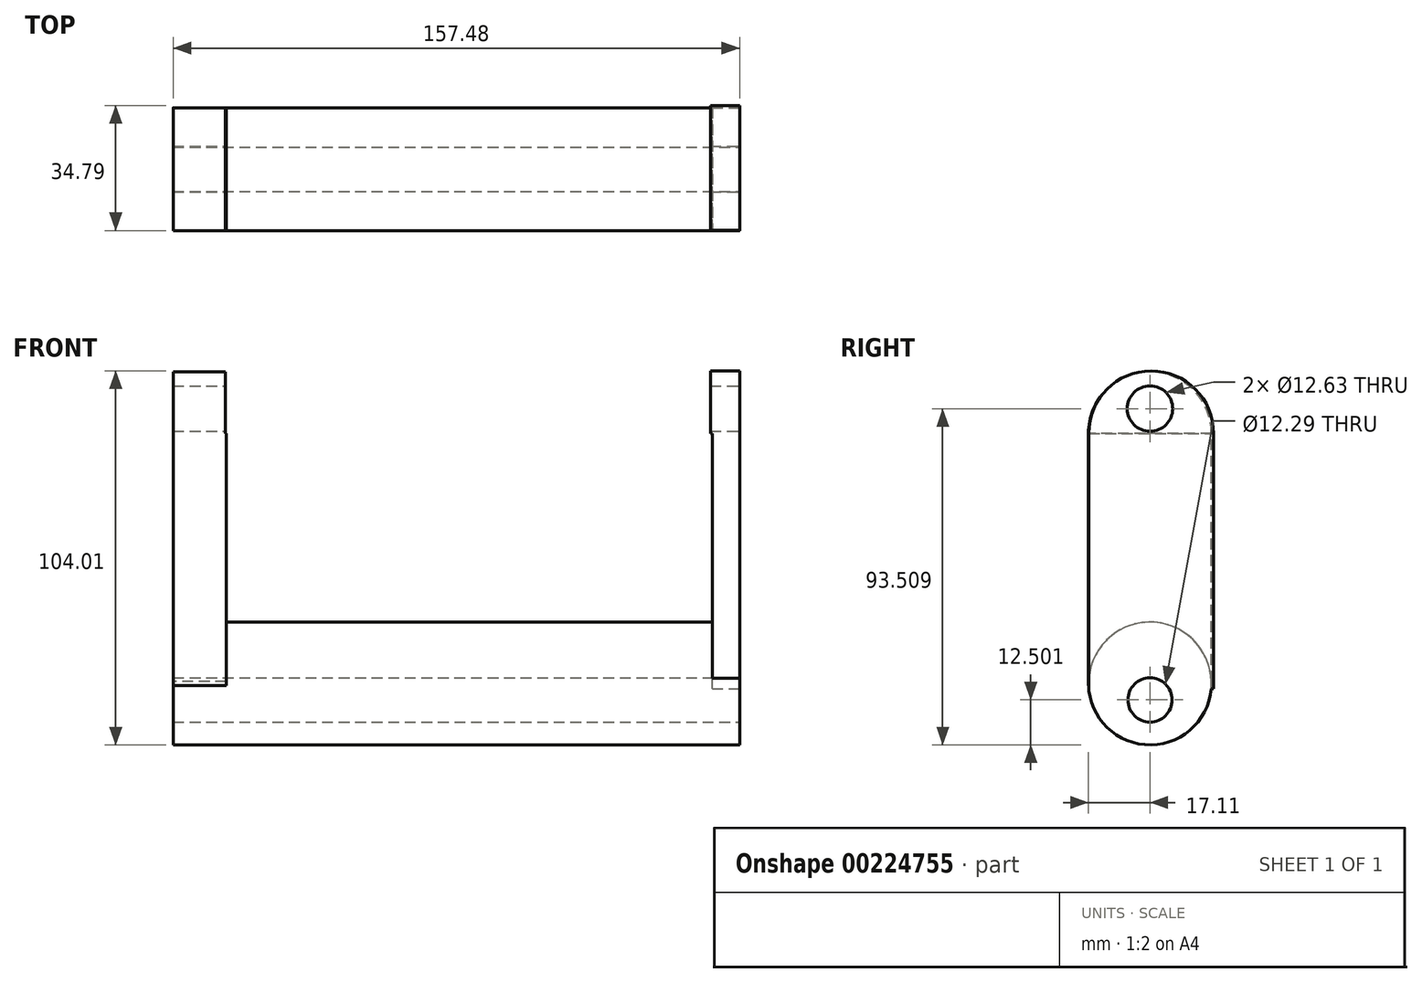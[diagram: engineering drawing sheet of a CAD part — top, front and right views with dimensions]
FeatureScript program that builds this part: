
annotation { "Feature Type Name" : "Feature", "Feature Type Description" : "" }
export const myFeature = defineFeature(function(context is Context, id is Id, definition is map)
    precondition{}
    {
        {
            var Q0;
            Q0=qCreatedBy(makeId("Right.planeOp"),FACE);
            var sketch = newSketch(context, id + "F0", { "sketchPlane" : qUnion([Q0])});
            skCircle(sketch, "E0", {"center": v(0, -44.93) * mm, "radius": 17.07 * mm});
            skSolve(sketch);
        }
        {
            var Q0;
            Q0=makeQuery(id+"F0.imprint","IMPRINT",FACE,{"disambiguationData":[TD([[makeQuery(id+"F0.imprint","IMPRINT",EDGE,{"derivedFrom":sQuery(id+"F0.wireOp",EDGE,"E0")}),1.0]])]});
            extrude(context, id + "F1", {"entities" : qUnion([Q0]), "endBound" : BoundingType.SYMMETRIC, "oppositeDirection" : true, "depth" : 149.35 * mm});
        }
        {
            var Q0;
            Q0=makeQuery(id+"F1.opExtrude","CAP_FACE",FACE,{"disambiguationData":[OSD([sQuery(id+"F0.wireOp",EDGE,"E0")])],"isStart":true});
            var sketch = newSketch(context, id + "F2", { "sketchPlane" : qUnion([Q0])});
            skLineSegment(sketch, "E1.bottom", {"start": v(-17.01, -46.34) * mm, "end": v(17.68, -46.34) * mm});
            skLineSegment(sketch, "E1.top", {"start": v(-17.01, 24.67) * mm, "end": v(17.68, 24.67) * mm});
            skLineSegment(sketch, "E1.left", {"start": v(-17.01, -46.34) * mm, "end": v(-17.01, 24.67) * mm});
            skLineSegment(sketch, "E1.right", {"start": v(17.68, -46.34) * mm, "end": v(17.68, 24.67) * mm});
            skSolve(sketch);
        }
        {
            var Q0;
            {var subQ2=sQuery(id+"F2.wireOp",EDGE,"E1.top");Q0=makeQuery(id+"F2.imprint","IMPRINT",FACE,{"disambiguationData":[TD([[makeQuery(id+"F2.imprint","IMPRINT",EDGE,{"derivedFrom":subQ2}),-1.0]])]});}
            extrude(context, id + "F3", {"entities" : qUnion([Q0]), "operationType" : NewBodyOperationType.ADD, "oppositeDirection" : true, "depth" : 7.62 * mm});
        }
        {
            var Q0;
            {var subQ0=sQuery(id+"F0.wireOp",EDGE,"E0");Q0=makeQuery(id+"F3.boolean.opBoolean","MERGE",FACE,{"derivedFrom":[makeQuery(id+"F1.opExtrude","CAP_FACE",FACE,{"disambiguationData":[OSD([subQ0])],"isStart":true}),makeQuery(id+"F3.opExtrude","CAP_FACE",FACE,{"disambiguationData":[OSD([subQ0,sQuery(id+"F2.wireOp",EDGE,"E1.bottom"),sQuery(id+"F2.wireOp",EDGE,"E1.top"),sQuery(id+"F2.wireOp",EDGE,"E1.left"),sQuery(id+"F2.wireOp",EDGE,"E1.right")])],"isStart":true})]});}
            var sketch = newSketch(context, id + "F4", { "sketchPlane" : qUnion([Q0])});
            skArc(sketch, "E2", {"start": v(17.68, 24.67) * mm, "mid": v(0.34, 42.02) * mm, "end": v(-17.01, 24.67) * mm});
            skSolve(sketch);
        }
        {
            var Q0;
            Q0=makeQuery(id+"F4.imprint","IMPRINT",FACE,{"disambiguationData":[TD([[makeQuery(id+"F4.imprint","IMPRINT",EDGE,{"derivedFrom":sQuery(id+"F4.wireOp",EDGE,"E2")}),1.0]])]});
            var Q1;
            Q1=makeQuery(id+"F1.opExtrude","CAP_FACE",FACE,{"disambiguationData":[OSD([sQuery(id+"F0.wireOp",EDGE,"E0")])],"isStart":false});
            extrude(context, id + "F5", {"entities" : qUnion([Q0, Q1]), "operationType" : NewBodyOperationType.ADD, "oppositeDirection" : true, "depth" : 8.13 * mm});
        }
        {
            var Q0;
            Q0=makeQuery(id+"F5.opExtrude","CAP_FACE",FACE,{"disambiguationData":[OSD([sQuery(id+"F0.wireOp",EDGE,"E0")])],"isStart":false});
            var sketch = newSketch(context, id + "F6", { "sketchPlane" : qUnion([Q0])});
            skLineSegment(sketch, "E3.bottom", {"start": v(-17.06, -45.47) * mm, "end": v(17.11, -45.47) * mm});
            skLineSegment(sketch, "E3.top", {"start": v(-17.06, 24.67) * mm, "end": v(17.11, 24.67) * mm});
            skLineSegment(sketch, "E3.left", {"start": v(-17.06, -45.47) * mm, "end": v(-17.06, 24.67) * mm});
            skLineSegment(sketch, "E3.right", {"start": v(17.11, -45.47) * mm, "end": v(17.11, 24.67) * mm});
            skSolve(sketch);
        }
        {
            var Q0;
            {var subQ1=sQuery(id+"F6.wireOp",EDGE,"E3.top");Q0=makeQuery(id+"F6.imprint","IMPRINT",FACE,{"disambiguationData":[TD([[makeQuery(id+"F6.imprint","IMPRINT",EDGE,{"derivedFrom":subQ1}),-1.0]])]});}
            extrude(context, id + "F7", {"entities" : qUnion([Q0]), "operationType" : NewBodyOperationType.ADD, "oppositeDirection" : true, "depth" : 14.73 * mm});
        }
        {
            var Q0;
            {var subQ0=sQuery(id+"F0.wireOp",EDGE,"E0");Q0=makeQuery(id+"F7.boolean.opBoolean","MERGE",FACE,{"derivedFrom":[makeQuery(id+"F5.opExtrude","CAP_FACE",FACE,{"disambiguationData":[OSD([subQ0])],"isStart":false}),makeQuery(id+"F7.opExtrude","CAP_FACE",FACE,{"disambiguationData":[OSD([subQ0,sQuery(id+"F6.wireOp",EDGE,"E3.bottom"),sQuery(id+"F6.wireOp",EDGE,"E3.top"),sQuery(id+"F6.wireOp",EDGE,"E3.left"),sQuery(id+"F6.wireOp",EDGE,"E3.right")])],"isStart":true})]});}
            var sketch = newSketch(context, id + "F8", { "sketchPlane" : qUnion([Q0])});
            skArc(sketch, "E4", {"start": v(17.11, 24.67) * mm, "mid": v(0.03, 41.76) * mm, "end": v(-17.06, 24.67) * mm});
            skSolve(sketch);
        }
        {
            var Q0;
            Q0=makeQuery(id+"F8.imprint","IMPRINT",FACE,{"disambiguationData":[TD([[makeQuery(id+"F8.imprint","IMPRINT",EDGE,{"derivedFrom":sQuery(id+"F8.wireOp",EDGE,"E4")}),1.0]])]});
            extrude(context, id + "F9", {"entities" : qUnion([Q0]), "operationType" : NewBodyOperationType.ADD, "oppositeDirection" : true, "depth" : 14.48 * mm});
        }
        {
            var Q0;
            {var subQ0=sQuery(id+"F2.wireOp",EDGE,"E1.top");var subQ1=sQuery(id+"F0.wireOp",EDGE,"E0");Q0=makeQuery(id+"F5.boolean.opBoolean","MERGE",FACE,{"derivedFrom":[makeQuery(id+"F3.boolean.opBoolean","MERGE",FACE,{"derivedFrom":[makeQuery(id+"F1.opExtrude","CAP_FACE",FACE,{"disambiguationData":[OSD([subQ1])],"isStart":true}),makeQuery(id+"F3.opExtrude","CAP_FACE",FACE,{"disambiguationData":[OSD([subQ1,sQuery(id+"F2.wireOp",EDGE,"E1.bottom"),subQ0,sQuery(id+"F2.wireOp",EDGE,"E1.left"),sQuery(id+"F2.wireOp",EDGE,"E1.right")])],"isStart":true})]}),makeQuery(id+"F5.opExtrude","CAP_FACE",FACE,{"disambiguationData":[OSD([subQ0,sQuery(id+"F4.wireOp",EDGE,"E2")])],"isStart":true})]});}
            var sketch = newSketch(context, id + "F10", { "sketchPlane" : qUnion([Q0])});
            skCircle(sketch, "E5", {"center": v(0, -49.49) * mm, "radius": 6.14 * mm});
            skSolve(sketch);
        }
        {
            var Q0;
            Q0=makeQuery(id+"F10.imprint","IMPRINT",FACE,{"disambiguationData":[TD([[makeQuery(id+"F10.imprint","IMPRINT",EDGE,{"derivedFrom":sQuery(id+"F10.wireOp",EDGE,"E5")}),1.0]])]});
            extrude(context, id + "F11", {"entities" : qUnion([Q0]), "operationType" : NewBodyOperationType.REMOVE, "endBound" : BoundingType.THROUGH_ALL, "oppositeDirection" : true, "depth" : 25.4 * mm});
        }
        {
            var Q0;
            {var subQ0=sQuery(id+"F2.wireOp",EDGE,"E1.top");var subQ1=sQuery(id+"F0.wireOp",EDGE,"E0");Q0=makeQuery(id+"F5.boolean.opBoolean","MERGE",FACE,{"derivedFrom":[makeQuery(id+"F3.boolean.opBoolean","MERGE",FACE,{"derivedFrom":[makeQuery(id+"F1.opExtrude","CAP_FACE",FACE,{"disambiguationData":[OSD([subQ1])],"isStart":true}),makeQuery(id+"F3.opExtrude","CAP_FACE",FACE,{"disambiguationData":[OSD([subQ1,sQuery(id+"F2.wireOp",EDGE,"E1.bottom"),subQ0,sQuery(id+"F2.wireOp",EDGE,"E1.left"),sQuery(id+"F2.wireOp",EDGE,"E1.right")])],"isStart":true})]}),makeQuery(id+"F5.opExtrude","CAP_FACE",FACE,{"disambiguationData":[OSD([subQ0,sQuery(id+"F4.wireOp",EDGE,"E2")])],"isStart":true})]});}
            var sketch = newSketch(context, id + "F12", { "sketchPlane" : qUnion([Q0])});
            skCircle(sketch, "E6", {"center": v(0, 31.52) * mm, "radius": 6.31 * mm});
            skSolve(sketch);
        }
        {
            var Q0;
            Q0=makeQuery(id+"F12.imprint","IMPRINT",FACE,{"disambiguationData":[TD([[makeQuery(id+"F12.imprint","IMPRINT",EDGE,{"derivedFrom":sQuery(id+"F12.wireOp",EDGE,"E6")}),1.0]])]});
            extrude(context, id + "F13", {"entities" : qUnion([Q0]), "operationType" : NewBodyOperationType.REMOVE, "endBound" : BoundingType.THROUGH_ALL, "oppositeDirection" : true, "depth" : 25.4 * mm});
        }
    });
